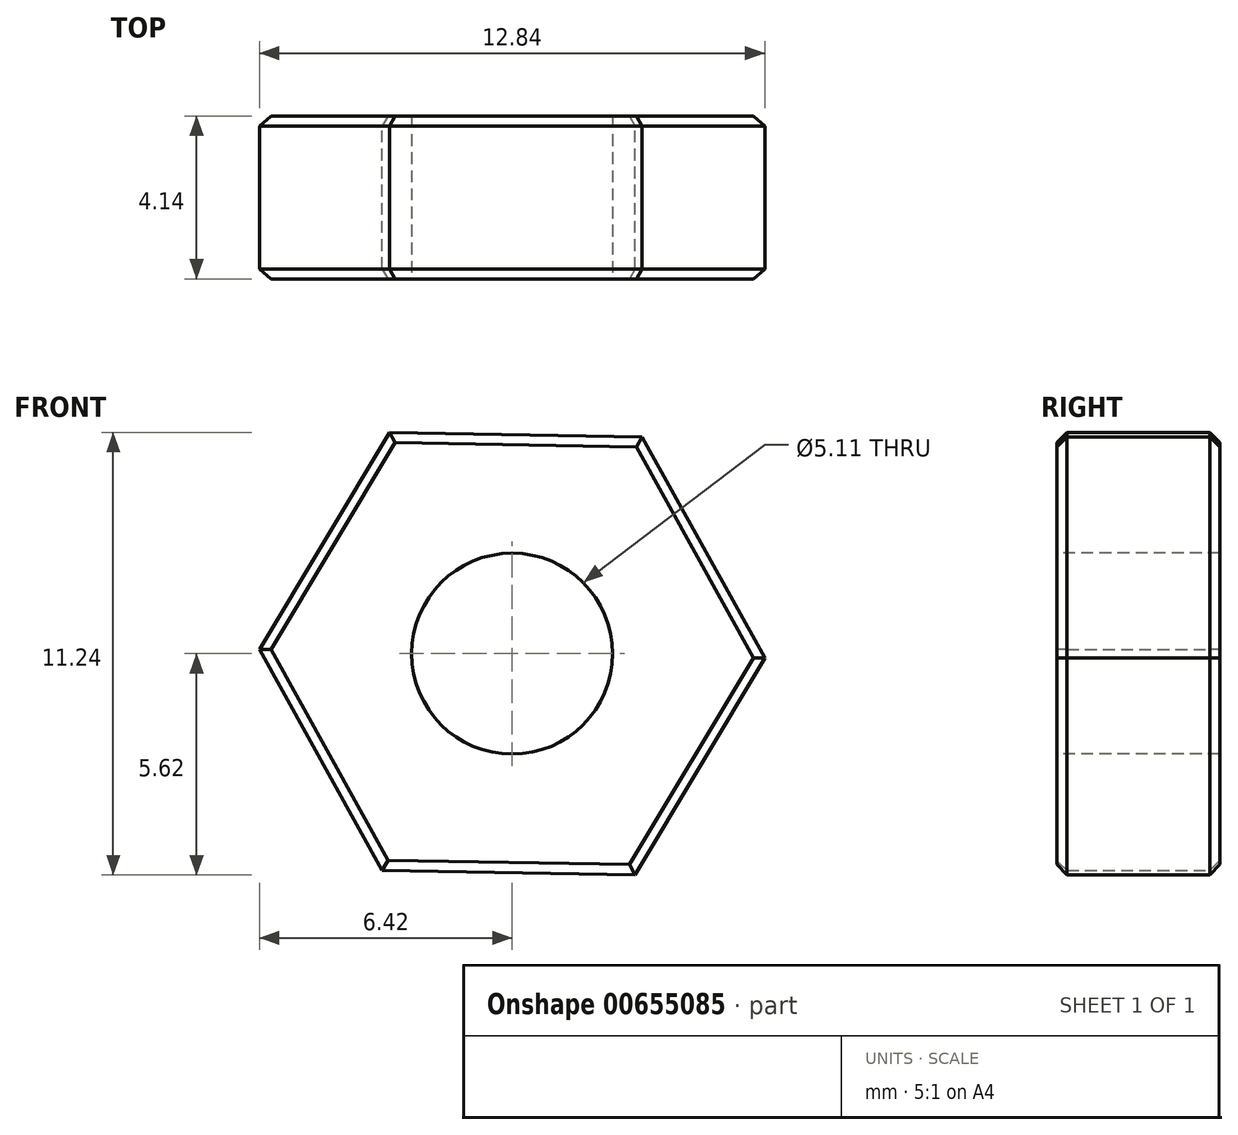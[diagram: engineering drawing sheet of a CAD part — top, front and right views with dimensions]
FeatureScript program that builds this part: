
annotation { "Feature Type Name" : "Feature", "Feature Type Description" : "" }
export const myFeature = defineFeature(function(context is Context, id is Id, definition is map)
    precondition{}
    {
        {
            var Q0;
            Q0=qCreatedBy(makeId("Front.planeOp"),FACE);
            var sketch = newSketch(context, id + "F0", { "sketchPlane" : qUnion([Q0])});
            skCircle(sketch, "E0.cCircle", {"center": v(0, 0) * mm, "radius": 5.56 * mm, "construction": true});
            skLineSegment(sketch, "E0.0", {"start": v(-6.42, 0.1) * mm, "end": v(-3.12, 5.62) * mm});
            skLineSegment(sketch, "E0.1", {"start": v(-3.12, 5.62) * mm, "end": v(3.3, 5.5) * mm});
            skLineSegment(sketch, "E0.2", {"start": v(3.3, 5.5) * mm, "end": v(6.42, -0.1) * mm});
            skLineSegment(sketch, "E0.3", {"start": v(6.42, -0.1) * mm, "end": v(3.12, -5.62) * mm});
            skLineSegment(sketch, "E0.4", {"start": v(3.12, -5.62) * mm, "end": v(-3.3, -5.5) * mm});
            skLineSegment(sketch, "E0.5", {"start": v(-3.3, -5.5) * mm, "end": v(-6.42, 0.1) * mm});
            skPoint(sketch, "E0.0.midPoint", {"position": v(-4.77, 2.86) * mm});
            skSolve(sketch);
        }
        {
            var Q0;
            Q0 = qSketchRegion(id + "F0", true);
            extrude(context, id + "F1", {"entities" : qUnion([Q0]), "depth" : 4.14 * mm, "offsetDistance" : 25.4 * mm});
        }
        {
            var Q0;
            Q0=makeQuery(id+"F1.opExtrude","CAP_FACE",FACE,{"disambiguationData":[OSD([sQuery(id+"F0.wireOp",EDGE,"E0.0"),sQuery(id+"F0.wireOp",EDGE,"E0.1"),sQuery(id+"F0.wireOp",EDGE,"E0.2"),sQuery(id+"F0.wireOp",EDGE,"E0.3"),sQuery(id+"F0.wireOp",EDGE,"E0.4"),sQuery(id+"F0.wireOp",EDGE,"E0.5")])],"isStart":false});
            var sketch = newSketch(context, id + "F2", { "sketchPlane" : qUnion([Q0])});
            skCircle(sketch, "E1", {"center": v(0, 0) * mm, "radius": 3.17 * mm});
            skSolve(sketch);
        }
        {
            var Q0;
            Q0=sQuery(id+"F2.wireOp",VERTEX,"E1.center");
            var Q1;
            Q1=makeQuery(id+"F1.opExtrude","SWEPT_BODY",BODY,{"disambiguationData":[OSD([sQuery(id+"F0.wireOp",EDGE,"E0.0"),sQuery(id+"F0.wireOp",EDGE,"E0.1"),sQuery(id+"F0.wireOp",EDGE,"E0.2"),sQuery(id+"F0.wireOp",EDGE,"E0.3"),sQuery(id+"F0.wireOp",EDGE,"E0.4"),sQuery(id+"F0.wireOp",EDGE,"E0.5")])]});
            hole(context, id + "F3", {"style" : HoleStyle.SIMPLE, "endStyle" : HoleEndStyle.THROUGH, "standardTappedOrClearance" : lookupTablePath({ "standard" : "ANSI", "engagement" : "75%", "pitch" : "20 tpi", "size" : "1/4", "type" : "Tapped" }), "standardBlindInLast" : lookupTablePath({ "standard" : "ANSI", "engagement" : "75%", "pitch" : "20 tpi", "size" : "1/4", "type" : "Tapped" }), "holeDiameter" : 5.1 * mm, "majorDiameter" : 6.35 * mm, "showTappedDepth" : true, "isTappedThrough" : true, "tappedDepth" : 11.6 * mm, "tapClearance" : 3, "startFromSketch" : true, "locations" : qUnion([Q0]), "scope" : qUnion([Q1])});
        }
        {
            var Q0;
            Q0=makeQuery(id+"F1.opExtrude","CAP_EDGE",EDGE,{"disambiguationData":[OSD([sQuery(id+"F0.wireOp",EDGE,"E0.0")])],"isStart":false});
            var Q1;
            Q1=makeQuery(id+"F1.opExtrude","CAP_EDGE",EDGE,{"disambiguationData":[OSD([sQuery(id+"F0.wireOp",EDGE,"E0.1")])],"isStart":false});
            var Q2;
            Q2=makeQuery(id+"F1.opExtrude","CAP_EDGE",EDGE,{"disambiguationData":[OSD([sQuery(id+"F0.wireOp",EDGE,"E0.2")])],"isStart":false});
            var Q3;
            Q3=makeQuery(id+"F1.opExtrude","CAP_EDGE",EDGE,{"disambiguationData":[OSD([sQuery(id+"F0.wireOp",EDGE,"E0.3")])],"isStart":false});
            var Q4;
            Q4=makeQuery(id+"F1.opExtrude","CAP_EDGE",EDGE,{"disambiguationData":[OSD([sQuery(id+"F0.wireOp",EDGE,"E0.4")])],"isStart":false});
            var Q5;
            Q5=makeQuery(id+"F1.opExtrude","CAP_EDGE",EDGE,{"disambiguationData":[OSD([sQuery(id+"F0.wireOp",EDGE,"E0.5")])],"isStart":false});
            var Q6;
            Q6=makeQuery(id+"F1.opExtrude","CAP_EDGE",EDGE,{"disambiguationData":[OSD([sQuery(id+"F0.wireOp",EDGE,"E0.5")])],"isStart":true});
            var Q7;
            Q7=makeQuery(id+"F1.opExtrude","CAP_EDGE",EDGE,{"disambiguationData":[OSD([sQuery(id+"F0.wireOp",EDGE,"E0.0")])],"isStart":true});
            var Q8;
            Q8=makeQuery(id+"F1.opExtrude","CAP_EDGE",EDGE,{"disambiguationData":[OSD([sQuery(id+"F0.wireOp",EDGE,"E0.1")])],"isStart":true});
            var Q9;
            Q9=makeQuery(id+"F1.opExtrude","CAP_EDGE",EDGE,{"disambiguationData":[OSD([sQuery(id+"F0.wireOp",EDGE,"E0.2")])],"isStart":true});
            var Q10;
            Q10=makeQuery(id+"F1.opExtrude","CAP_EDGE",EDGE,{"disambiguationData":[OSD([sQuery(id+"F0.wireOp",EDGE,"E0.3")])],"isStart":true});
            var Q11;
            Q11=makeQuery(id+"F1.opExtrude","CAP_EDGE",EDGE,{"disambiguationData":[OSD([sQuery(id+"F0.wireOp",EDGE,"E0.4")])],"isStart":true});
            chamfer(context, id + "F4", {"entities" : qUnion([Q0, Q1, Q2, Q3, Q4, Q5, Q6, Q7, Q8, Q9, Q10, Q11]), "width" : 0.25 * mm, "tangentPropagation" : true});
        }
    });
